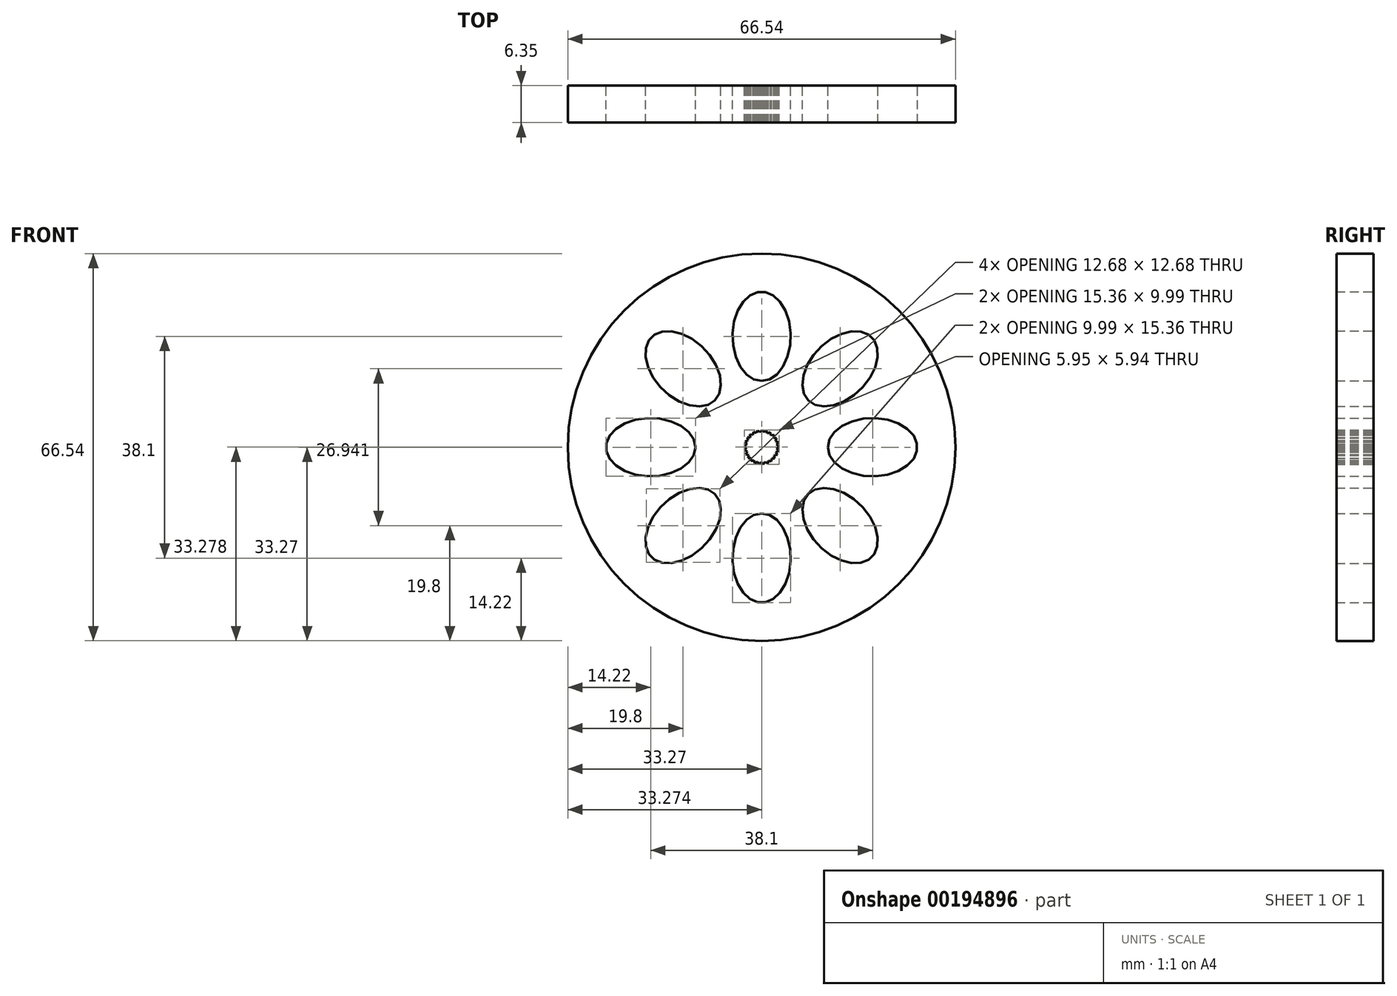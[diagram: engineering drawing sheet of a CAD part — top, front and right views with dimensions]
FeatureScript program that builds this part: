
annotation { "Feature Type Name" : "Feature", "Feature Type Description" : "" }
export const myFeature = defineFeature(function(context is Context, id is Id, definition is map)
    precondition{}
    {
        {
            var Q0;
            Q0=qCreatedBy(makeId("Front.planeOp"),FACE);
            var sketch = newSketch(context, id + "F0", { "sketchPlane" : qUnion([Q0])});
            skCircle(sketch, "E0", {"center": v(0, 0) * mm, "radius": 33.27 * mm});
            skEllipse(sketch, "E1", {"center": v(0, 19.05) * mm, "majorRadius": 7.68 * mm, "minorRadius": 5 * mm, "majorAxis": v(0, -1)});
            skEllipse(sketch, "E2.1.0", {"center": v(-13.47, 13.47) * mm, "majorRadius": 7.68 * mm, "minorRadius": 5 * mm, "majorAxis": v(0.7, -0.7)});
            skEllipse(sketch, "E2.2.0", {"center": v(-19.05, 0) * mm, "majorRadius": 7.68 * mm, "minorRadius": 5 * mm, "majorAxis": v(1, 0)});
            skEllipse(sketch, "E2.3.0", {"center": v(-13.47, -13.47) * mm, "majorRadius": 7.68 * mm, "minorRadius": 5 * mm, "majorAxis": v(0.7, 0.7)});
            skEllipse(sketch, "E2.4.0", {"center": v(0, -19.05) * mm, "majorRadius": 7.68 * mm, "minorRadius": 5 * mm, "majorAxis": v(0, 1)});
            skEllipse(sketch, "E2.5.0", {"center": v(13.47, -13.47) * mm, "majorRadius": 7.68 * mm, "minorRadius": 5 * mm, "majorAxis": v(-0.7, 0.7)});
            skEllipse(sketch, "E2.6.0", {"center": v(19.05, 0) * mm, "majorRadius": 7.68 * mm, "minorRadius": 5 * mm, "majorAxis": v(-1, 0)});
            skEllipse(sketch, "E2.7.0", {"center": v(13.47, 13.47) * mm, "majorRadius": 7.68 * mm, "minorRadius": 5 * mm, "majorAxis": v(-0.7, -0.7)});
            skPoint(sketch, "E3.centerSnap0", {"position": v(-104.16, 0) * mm});
            skPoint(sketch, "E3.centerSnap1", {"position": v(0, -34.23) * mm});
            skLineSegment(sketch, "E4", {"start": v(-2.48, 1.65) * mm, "end": v(-2.31, 1.15) * mm});
            skLineSegment(sketch, "E5", {"start": v(-2.31, 1.15) * mm, "end": v(-2.81, 0.98) * mm});
            skLineSegment(sketch, "E6.1.0", {"start": v(-2.81, 0.98) * mm, "end": v(-2.53, 0.54) * mm});
            skLineSegment(sketch, "E6.1.1", {"start": v(-2.53, 0.54) * mm, "end": v(-2.97, 0.25) * mm});
            skLineSegment(sketch, "E6.2.0", {"start": v(-2.97, 0.25) * mm, "end": v(-2.58, -0.1) * mm});
            skLineSegment(sketch, "E6.2.1", {"start": v(-2.58, -0.1) * mm, "end": v(-2.94, -0.5) * mm});
            skLineSegment(sketch, "E6.3.0", {"start": v(-2.94, -0.5) * mm, "end": v(-2.47, -0.74) * mm});
            skLineSegment(sketch, "E6.3.1", {"start": v(-2.47, -0.74) * mm, "end": v(-2.72, -1.2) * mm});
            skLineSegment(sketch, "E6.4.0", {"start": v(-2.72, -1.2) * mm, "end": v(-2.21, -1.34) * mm});
            skLineSegment(sketch, "E6.4.1", {"start": v(-2.21, -1.34) * mm, "end": v(-2.34, -1.85) * mm});
            skLineSegment(sketch, "E6.5.0", {"start": v(-2.34, -1.85) * mm, "end": v(-1.8, -1.84) * mm});
            skLineSegment(sketch, "E6.5.1", {"start": v(-1.8, -1.84) * mm, "end": v(-1.8, -2.37) * mm});
            skLineSegment(sketch, "E6.6.0", {"start": v(-1.8, -2.37) * mm, "end": v(-1.3, -2.24) * mm});
            skLineSegment(sketch, "E6.6.1", {"start": v(-1.3, -2.24) * mm, "end": v(-1.16, -2.75) * mm});
            skLineSegment(sketch, "E6.7.0", {"start": v(-1.16, -2.75) * mm, "end": v(-0.7, -2.49) * mm});
            skLineSegment(sketch, "E6.7.1", {"start": v(-0.7, -2.49) * mm, "end": v(-0.44, -2.95) * mm});
            skLineSegment(sketch, "E6.8.0", {"start": v(-0.44, -2.95) * mm, "end": v(-0.06, -2.58) * mm});
            skLineSegment(sketch, "E6.8.1", {"start": v(-0.06, -2.58) * mm, "end": v(0.3, -2.96) * mm});
            skLineSegment(sketch, "E6.9.0", {"start": v(0.3, -2.96) * mm, "end": v(0.59, -2.52) * mm});
            skLineSegment(sketch, "E6.9.1", {"start": v(0.59, -2.52) * mm, "end": v(1.04, -2.8) * mm});
            skLineSegment(sketch, "E6.10.0", {"start": v(1.04, -2.8) * mm, "end": v(1.2, -2.3) * mm});
            skLineSegment(sketch, "E6.10.1", {"start": v(1.2, -2.3) * mm, "end": v(1.7, -2.45) * mm});
            skLineSegment(sketch, "E6.11.0", {"start": v(1.7, -2.45) * mm, "end": v(1.73, -1.92) * mm});
            skLineSegment(sketch, "E6.11.1", {"start": v(1.73, -1.92) * mm, "end": v(2.25, -1.95) * mm});
            skLineSegment(sketch, "E6.12.0", {"start": v(2.25, -1.95) * mm, "end": v(2.15, -1.43) * mm});
            skLineSegment(sketch, "E6.12.1", {"start": v(2.15, -1.43) * mm, "end": v(2.67, -1.33) * mm});
            skLineSegment(sketch, "E6.13.0", {"start": v(2.67, -1.33) * mm, "end": v(2.44, -0.85) * mm});
            skLineSegment(sketch, "E6.13.1", {"start": v(2.44, -0.85) * mm, "end": v(2.91, -0.62) * mm});
            skLineSegment(sketch, "E6.14.0", {"start": v(2.91, -0.62) * mm, "end": v(2.57, -0.22) * mm});
            skLineSegment(sketch, "E6.14.1", {"start": v(2.57, -0.22) * mm, "end": v(2.98, 0.12) * mm});
            skLineSegment(sketch, "E6.15.0", {"start": v(2.98, 0.12) * mm, "end": v(2.55, 0.43) * mm});
            skLineSegment(sketch, "E6.15.1", {"start": v(2.55, 0.43) * mm, "end": v(2.85, 0.86) * mm});
            skLineSegment(sketch, "E6.16.0", {"start": v(2.85, 0.86) * mm, "end": v(2.36, 1.05) * mm});
            skLineSegment(sketch, "E6.16.1", {"start": v(2.36, 1.05) * mm, "end": v(2.55, 1.54) * mm});
            skLineSegment(sketch, "E6.17.0", {"start": v(2.55, 1.54) * mm, "end": v(2.03, 1.6) * mm});
            skLineSegment(sketch, "E6.17.1", {"start": v(2.03, 1.6) * mm, "end": v(2.09, 2.13) * mm});
            skLineSegment(sketch, "E6.18.0", {"start": v(2.09, 2.13) * mm, "end": v(1.56, 2.06) * mm});
            skLineSegment(sketch, "E6.18.1", {"start": v(1.56, 2.06) * mm, "end": v(1.5, 2.58) * mm});
            skLineSegment(sketch, "E6.19.0", {"start": v(1.5, 2.58) * mm, "end": v(1, 2.38) * mm});
            skLineSegment(sketch, "E6.19.1", {"start": v(1, 2.38) * mm, "end": v(0.8, 2.87) * mm});
            skLineSegment(sketch, "E6.20.0", {"start": v(0.8, 2.87) * mm, "end": v(0.38, 2.56) * mm});
            skLineSegment(sketch, "E6.20.1", {"start": v(0.38, 2.56) * mm, "end": v(0.07, 2.98) * mm});
            skLineSegment(sketch, "E6.21.0", {"start": v(0.07, 2.98) * mm, "end": v(-0.27, 2.57) * mm});
            skLineSegment(sketch, "E6.21.1", {"start": v(-0.27, 2.57) * mm, "end": v(-0.68, 2.9) * mm});
            skLineSegment(sketch, "E6.22.0", {"start": v(-0.68, 2.9) * mm, "end": v(-0.9, 2.42) * mm});
            skLineSegment(sketch, "E6.22.1", {"start": v(-0.9, 2.42) * mm, "end": v(-1.38, 2.64) * mm});
            skLineSegment(sketch, "E6.23.0", {"start": v(-1.38, 2.64) * mm, "end": v(-1.47, 2.12) * mm});
            skLineSegment(sketch, "E6.23.1", {"start": v(-1.47, 2.12) * mm, "end": v(-2, 2.22) * mm});
            skLineSegment(sketch, "E6.24.0", {"start": v(-2, 2.22) * mm, "end": v(-1.95, 1.69) * mm});
            skLineSegment(sketch, "E6.24.1", {"start": v(-1.95, 1.69) * mm, "end": v(-2.48, 1.65) * mm});
            skSolve(sketch);
        }
        {
            var Q0;
            Q0=makeQuery(id+"F0.imprint","IMPRINT",FACE,{"disambiguationData":[TD([[makeQuery(id+"F0.imprint","IMPRINT",EDGE,{"derivedFrom":sQuery(id+"F0.wireOp",EDGE,"E0")}),1.0]])]});
            extrude(context, id + "F1", {"entities" : qUnion([Q0]), "depth" : 6.35 * mm});
        }
    });
